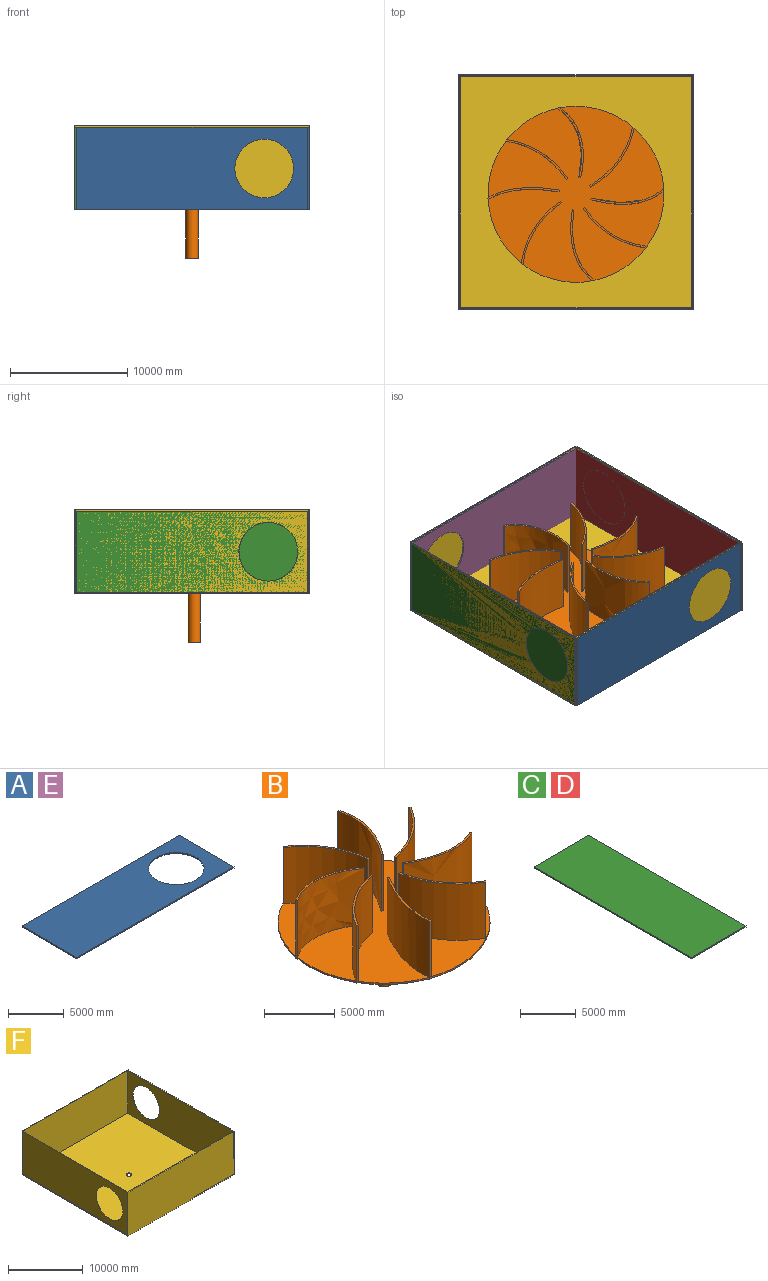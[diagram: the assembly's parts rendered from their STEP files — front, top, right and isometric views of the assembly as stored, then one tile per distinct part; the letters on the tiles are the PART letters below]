
ASSEMBLY  parts=6 mates=5
PART A: 7 faces, bbox 20000x7000x127 mm
  f0: plane 20000x127mm, normal (0,1,0), area 2540000mm2, adj f1,f4,f5,f6
  f1: plane 7000x127mm, normal (-1,0,0), area 889000mm2, adj f0,f2,f5,f6
  f2: plane 20000x127mm, normal (0,-1,0), area 2540000mm2, adj f1,f4,f5,f6
  f3: cylinder r=2500mm len=5000mm, axis (0,0,-1), area 1994911.3mm2, adj f5,f6
  f4: plane 7000x127mm, normal (1,0,0), area 889000mm2, adj f0,f2,f5,f6
  f5: plane 20000x7000mm, normal (0,0,1), area 120365045.9mm2, adj f0,f1,f2,f3,f4
  f6: plane 20000x7000mm, normal (0,0,-1), area 120365045.9mm2, adj f0,f1,f2,f3,f4
PART B: 48 faces, bbox 14995.2x14995.2x10130.8 mm
  f0: plane 4873x148.86mm, normal (-0.19,0.98,0), area 738493.9mm2, adj f1,f3,f4,f5
  f1: cylinder r=7500mm len=5089.64mm, axis (0,0,-1), area 31382478.3mm2, adj f0,f2,f4,f5
  f2: plane 4873x131.24mm, normal (0.87,-0.5,0), area 738493.9mm2, adj f1,f3,f4,f5
  f3: cylinder r=7348.45mm len=4986.8mm, axis (0,0,-1), area 30748351mm2, adj f0,f2,f4,f5
  f4: plane 5118.04x3692.89mm, normal (0,0,1), area 966120.4mm2, adj f0,f1,f2,f3
  f5: plane 14995.25x14995.25mm, normal (0,0,1), area 168850224.7mm2, adj f0,f1,f2,f3,f6,f7,f8,f9
  f6: plane 4873x130.65mm, normal (-0.86,0.51,0), area 738494.1mm2, adj f5,f7,f9,f10
  f7: extruded ~6171x4873mm, area 31672990.3mm2, adj f5,f6,f8,f10
  f8: plane 4873x133.93mm, normal (0.88,0.47,0), area 738493.9mm2, adj f5,f7,f9,f10
  f9: extruded ~6023.28x4873mm, area 30920915.2mm2, adj f5,f6,f8,f10
  f10: plane 6171x1545.69mm, normal (0,0,1), area 973321.1mm2, adj f6,f7,f8,f9
  f11: plane 4873x148.86mm, normal (-0.98,-0.19,0), area 738493.9mm2, adj f5,f12,f14,f15
  f12: cylinder r=7500mm len=5089.64mm, axis (0,0,-1), area 31382478.3mm2, adj f5,f11,f13,f15
  f13: plane 4873x131.24mm, normal (0.5,0.87,0), area 738493.9mm2, adj f5,f12,f14,f15
  f14: cylinder r=7348.45mm len=4986.8mm, axis (0,0,-1), area 30748351mm2, adj f5,f11,f13,f15
  f15: plane 5118.04x3692.89mm, normal (0,0,1), area 966120.4mm2, adj f11,f12,f13,f14
  f16: cylinder r=7497.62mm len=3907.52mm, axis (0,0,-1), area 655610.5mm2, adj f5,f38,f42,f45
  f17: cylinder r=7497.62mm len=14995.25mm, axis (0,0,-1), area 3746990.3mm2, adj f5,f27,f43,f45
  f18: cylinder r=7497.62mm len=5038.78mm, axis (0,0,-1), area 662422.5mm2, adj f5,f33,f37,f45
  f19: cylinder r=7497.62mm len=5238.94mm, axis (0,0,-1), area 864935.5mm2, adj f5,f28,f32,f45
  f20: plane 4873x122.57mm, normal (-0.59,-0.81,0), area 738494mm2, adj f5,f21,f23,f24
  f21: extruded ~5960.35x4873mm, area 31265936.5mm2, adj f5,f20,f22,f24
  f22: plane 4873x184.05mm, normal (0.48,0.87,0), area 1025175.3mm2, adj f5,f21,f23,f24
  f23: extruded ~5973.13x4873mm, area 31320091.2mm2, adj f5,f20,f22,f24
  f24: plane 6062.26x1956.28mm, normal (0,0,1), area 973160.8mm2, adj f20,f21,f22,f23
  f25: plane 4873x150.45mm, normal (0.12,-0.99,0), area 738493.9mm2, adj f5,f26,f27,f29
  f26: cylinder r=7348.45mm len=5216.69mm, axis (0,0,-1), area 30748351mm2, adj f5,f25,f28,f29
  f27: cylinder r=7500mm len=5324.27mm, axis (0,0,-1), area 31384144.8mm2, adj f5,f17,f25,f28,f29,f45
  f28: plane 5000x125.78mm, normal (-0.83,0.56,0), area 741448.7mm2, adj f5,f19,f26,f27,f29,f45
  f29: plane 5342.47x3346.46mm, normal (0,0,1), area 966120.4mm2, adj f25,f26,f27,f28
  f30: plane 4873x122.72mm, normal (0.81,-0.59,0), area 738493.9mm2, adj f5,f31,f32,f34
  f31: extruded ~6098.47x4873mm, area 31986306.4mm2, adj f5,f30,f33,f34
  f32: extruded ~6282.36x5000mm, area 32961365mm2, adj f5,f19,f30,f33,f34,f45
  f33: plane 5000x118.1mm, normal (-0.78,-0.63,0), area 748763.4mm2, adj f5,f18,f31,f32,f34,f45
  f34: plane 6282.36x1752.77mm, normal (0,0,1), area 1009738mm2, adj f30,f31,f32,f33
  f35: plane 4873x148.86mm, normal (0.98,0.19,0), area 738493.9mm2, adj f5,f36,f37,f39
  f36: cylinder r=7348.45mm len=4986.8mm, axis (0,0,-1), area 30748351mm2, adj f5,f35,f38,f39
  f37: cylinder r=7500mm len=5089.64mm, axis (0,0,-1), area 31392548.7mm2, adj f5,f18,f35,f38,f39,f45
  f38: plane 5000x131.24mm, normal (-0.5,-0.87,0), area 756136.4mm2, adj f5,f16,f36,f37,f39,f45
  f39: plane 5118.04x3692.89mm, normal (0,0,1), area 966120.4mm2, adj f35,f36,f37,f38
  f40: plane 4873x128.75mm, normal (0.53,0.85,0), area 738494mm2, adj f5,f41,f42,f44
  f41: extruded ~5820.06x4873mm, area 30076675.3mm2, adj f5,f40,f43,f44
  f42: extruded ~5922.54x5000mm, area 30603626.2mm2, adj f5,f16,f40,f43,f44,f45
  f43: plane 5000x149.9mm, normal (0.15,-0.99,0), area 750682.9mm2, adj f5,f17,f41,f42,f44,f45
  f44: plane 5922.54x1859.99mm, normal (0,0,1), area 943465.5mm2, adj f40,f41,f42,f43
  f45: plane 14995.25x14995.25mm, normal (0,0,-1), area 175734570.6mm2, adj f16,f17,f18,f19,f27,f28,f32,f33
  f46: cylinder r=529.2mm len=5130.8mm, axis (0,0,1), area 17060321.8mm2, adj f45,f47
  f47: plane 1058.41x1058.41mm, normal (0,0,-1), area 879821.2mm2, adj f46
PART C: 6 faces, bbox 7000x20000x127 mm
  f0: plane 7000x127mm, normal (0,1,0), area 889000mm2, adj f2,f3,f4,f5
  f1: plane 7000x127mm, normal (0,-1,0), area 889000mm2, adj f2,f3,f4,f5
  f2: plane 20000x127mm, normal (1,0,0), area 2540000mm2, adj f0,f1,f3,f4
  f3: plane 20000x7000mm, normal (0,0,1), area 140000000mm2, adj f0,f1,f2,f5
  f4: plane 20000x7000mm, normal (0,0,-1), area 140000000mm2, adj f0,f1,f2,f5
  f5: plane 20000x127mm, normal (-1,0,0), area 2540000mm2, adj f0,f1,f3,f4
PART D: same geometry as C
PART E: same geometry as A
PART F: 14 faces, bbox 20000x20000x7127 mm
  f0: plane 19881.41x19874.83mm, normal (0,0,1), area 394649747.8mm2, adj f5,f7,f8,f9,f10
  f1: plane 20000x7127mm, normal (0,1,0), area 142540000mm2, adj f2,f4,f6,f11
  f2: plane 20000x7127mm, normal (-1,0,0), area 122905045.9mm2, adj f1,f3,f6,f11,f13
  f3: plane 20000x7127mm, normal (0,-1,0), area 142540000mm2, adj f2,f4,f6,f11
  f4: plane 20000x7127mm, normal (1,0,0), area 122905045.9mm2, adj f1,f3,f6,f11,f12
  f5: cylinder r=394.94mm len=789.87mm, axis (0,0,-1), area 315144.8mm2, adj f0,f6
  f6: plane 20000x20000mm, normal (0,0,-1), area 399509992.3mm2, adj f1,f2,f3,f4,f5
  f7: plane 19874.83x7000mm, normal (1,0,0), area 119488864.3mm2, adj f0,f8,f10,f11,f13
  f8: plane 19881.41x7000mm, normal (0,-1,0), area 139169900.9mm2, adj f0,f7,f9,f11
  f9: plane 19874.83x7000mm, normal (-1,0,0), area 119488864.3mm2, adj f0,f8,f10,f11,f12
  f10: plane 19881.41x7000mm, normal (0,1,0), area 139169900.9mm2, adj f0,f7,f9,f11
  f11: plane 20000x20000mm, normal (0,0,1), area 4860244.5mm2, adj f1,f2,f3,f4,f7,f8,f9,f10
  f12: cylinder r=2500mm len=5000mm, axis (1,0,0), area 1214376.5mm2, adj f4,f9
  f13: cylinder r=2500mm len=5000mm, axis (-1,0,0), area 648361.5mm2, adj f2,f7
PLACE A rot(axis=(1,0,0),90deg) t=(-3421.62,-8936.42,249.55)mm
PLACE B rot(axis=(0,0,-1),68deg) t=(-4057.21,744.19,-2758.1)mm
PLACE C rot(axis=(-0.71,0,-0.71),180deg) t=(-14057.21,10700.15,-6213.03)mm
PLACE D rot(axis=(0,1,0),90deg) t=(5815.79,-8826.99,5696.83)mm
PLACE E rot(axis=(0,-0.71,-0.71),180deg) t=(-4692.81,10809.58,249.55)mm
PLACE F t=(-4057.21,744.19,-3758.1)mm fixed
MATE fastened C.f4 <-> F.f2  axis (-1,0,0) through (-14057.21,936.58,-3758.1)mm
MATE fastened A.f5 <-> F.f3  axis (0,-1,0) through (-4057.21,-9063.42,-3758.1)mm
MATE fastened F.f4 <-> D.f3  axis (1,0,0) through (5942.79,936.58,-3758.1)mm
MATE fastened C.f1 <-> E.f5  axis (0,1,0) through (-14057.21,10936.58,-258.1)mm
MATE revolute F.f5 <-> B.f16  axis (0,0,-1) through (-4057.21,744.19,-3758.1)mm
